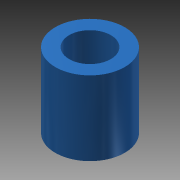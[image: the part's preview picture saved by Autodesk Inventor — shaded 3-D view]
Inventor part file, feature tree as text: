
AUTODESK INVENTOR PART (.ipt)
format: ipt  version: 2013 SP2 (Build 170200200, 200)  size: 84,480 bytes
history: native  units: mm
features: extrude x2, sketch x2
ambient origin geometry x8: Origin, YZ Plane, XZ Plane, XY Plane, X Axis, Y Axis, Z Axis, Center Point
bodies: Solid1 (feature_tree)
feature tree (4):
  extrude  "Extrusion1"  Depth=7.0mm
  extrude  "Extrusion2"  Depth=5.9mm
  sketch  "Sketch1"  dims[d0=4.2mm d1=7.0mm]
  sketch  "Sketch2"  dims[d2=7.5mm d3=0.0mm d4=5.9mm d5=1.8mm d6=0.0mm]
